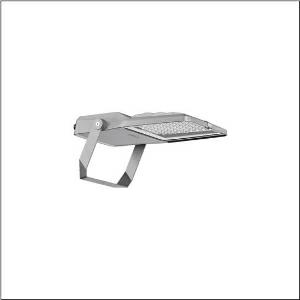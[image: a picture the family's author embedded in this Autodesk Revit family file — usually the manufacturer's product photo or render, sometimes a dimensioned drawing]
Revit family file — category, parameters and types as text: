
# Revit family: floodlight_fl_21_iq_mini___pl64_5xa7771d2e1a_0f9a
name_source: partatom
category: Lighting Fixtures
units: mm (PartAtom-declared; Revit-internal decimal feet)

## family parameters
Cut with Voids When Loaded = No
Host = Face
Light Source = No
Part Type = Normal
Room Calculation Point = No
Round Connector Dimension = Use Diameter
Shared = No

## types (1)
- --- (1 x LED, 17220 lm, 143 W, 3000K)
    Apparent Load = 143 VA
    CIE Flux Codes = 28 80 98 100 100
    Color Rendering = 70
    Color Temperature = 3000K
    Default Elevation = 1800 mm
    Description = Floodlight FL 21 iQ mini, floodlight, primary light control with lens, of PMMA, primary optical cover: protective disc, of toughened safety glass, transparent, light distribution: PL64, light emission: direct distribution, installation type: surface-mounted, LED, High Power LED, rated luminous flux: 17.220lm, luminous efficacy: 120lm/W, light colour: 730, colour temperature: 3000K, control gear: iQ Comfort/DALI, control: Auto-Match, Temp-Guard, Lumen-Switch, Night-Set, Smart-Wire, Light-Fading, Desk-Remote (wireless, voltage-free reading and setting of iQ features in the workshop via application-optimized NFC function/RFID function), optimised constant luminous flux control (CLO 2.0), with terminal, 6-pole, mains connection: 220..240V, AC, 50/60Hz, start of lifetime: 143W, end of service life: 152W, reduction: 61W, luminaire housing, of diecast aluminium, powder-coated, Siteco® metallic grey (DB 702S), corrosivity category C5 mid according to DIN EN ISO 12944, suitable for swimming pools, chlorine-resistant, sealing non-destructively replaceable, mounting bracket, of steel, galvanised, powder-coated, Siteco® metallic grey (DB 702S), protection rating (complete): IP66, insulation class (complete): insulation class II (safety insulation), certification: CE, ENEC, VDE, protection symbol: D, impact resistance: IK08, permissible operating ambient temperature: -40..+40°C, permissible operating ambient temperature for outdoor applications: -40..+50°C, standard: DIN EN 12944, LABS conformity tested according to VDMA 24364:2018-05, packaging unit: 1 piece

Light Distribution: PL64
    Height = 70 mm
    Lamp = 1 x LED
    Lamp Light Flux = 17220 lm
    Lamp Power = 143 W
    Lamp count = 1
    Length = 485 mm
    Luminous efficacy = 120 lm/W
    Manufacturer = Siteco
    ModVariant = No
    Model = 5XA7771D2E1A
    Number of Poles = 1
    OnlyDefault = Yes
    Power Factor = 1
    Product Name = Floodlight FL 21 iQ mini | PL64
    Product group = floodlight | pylon annexe
    ProductGroupID = 6200
    Protection Class = Protection class II
    Protection Degree = IP 66
    RLX_Detail_Level = 1
    RLX_Emergency_Light_Flux = 0 lm
    RLX_Emergency_Type = 0
    RLX_Emergency_Type_DB = No
    RlxData = <blob elided: 96513 chars, md5=1867d88a>
    Socket = socket
    Standby Power = 0 W
    System Light Flux = 17220 lm
    System Power = 143 W
    Type Comments = factory setting: luminous flux: 100 % | dim-lin: 254 | 730 mA
    Type Image = l_1006845.jpg
    URL = http://relux.com
    VarID = @adj_166144
    Voltage = 0 V
    Weight = 0.00 kg
    Width = 337 mm

## geometry (parser evidence)
native form markers: Blend x4, Sweep x12
no freeform markers — native parametric forms only
